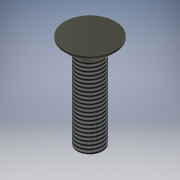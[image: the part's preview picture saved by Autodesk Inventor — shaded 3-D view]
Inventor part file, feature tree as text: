
AUTODESK INVENTOR PART (.ipt)
format: ipt  version: 2020.2 (Build 242310000, 310)  size: 130,560 bytes
history: native  units: mm
features: extrude x3, sketch x3, other x1, thread x1, chamfer x1
ambient origin geometry x1: Origin
bodies: Body1 (feature_tree)
feature tree (9):
  other  "ソリッド1"
  extrude  "押し出し1"  Depth=5.0mm
  extrude  "押し出し2"  Depth=6.0mm TaperAngle=0.0deg
  thread  "ねじ1"
  chamfer  "面取り1"  Distance=10.0mm
  extrude  "押し出し4"  Depth=2.8mm TaperAngle=0.0deg
  sketch  "スケッチ1"
  sketch  "スケッチ2"
  sketch  "スケッチ4"
